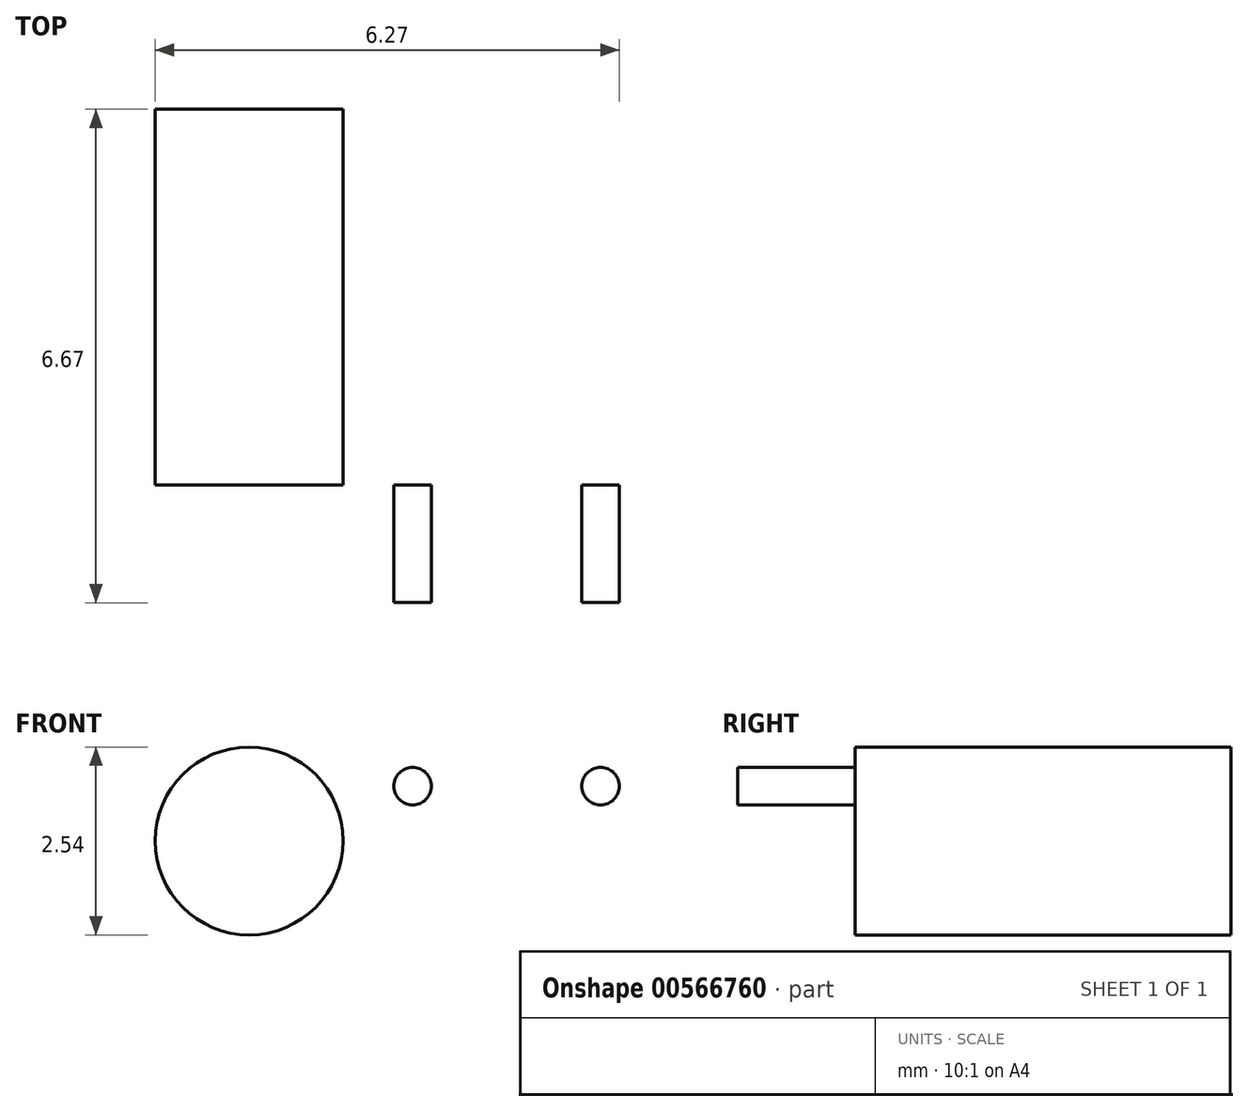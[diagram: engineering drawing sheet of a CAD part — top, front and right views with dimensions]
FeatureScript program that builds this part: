
annotation { "Feature Type Name" : "Feature", "Feature Type Description" : "" }
export const myFeature = defineFeature(function(context is Context, id is Id, definition is map)
    precondition{}
    {
        {
            var Q0;
            Q0=qCreatedBy(makeId("Front.planeOp"),FACE);
            var sketch = newSketch(context, id + "F0", { "sketchPlane" : qUnion([Q0])});
            skCircle(sketch, "E0", {"center": v(0, 0) * mm, "radius": 1.27 * mm});
            skCircle(sketch, "E1", {"center": v(2.2, 0.74) * mm, "radius": 0.25 * mm});
            skSolve(sketch);
        }
        {
            var Q0;
            Q0=makeQuery(id+"F0.imprint","IMPRINT",FACE,{"disambiguationData":[TD([[makeQuery(id+"F0.imprint","IMPRINT",EDGE,{"derivedFrom":sQuery(id+"F0.wireOp",EDGE,"E0")}),1.0]])]});
            extrude(context, id + "F1", {"entities" : qUnion([Q0]), "oppositeDirection" : true, "depth" : 5.08 * mm, "offsetDistance" : 25.4 * mm});
        }
        {
            var Q0;
            Q0=makeQuery(id+"F0.imprint","IMPRINT",FACE,{"disambiguationData":[TD([[makeQuery(id+"F0.imprint","IMPRINT",EDGE,{"derivedFrom":sQuery(id+"F0.wireOp",EDGE,"E1")}),1.0]])]});
            extrude(context, id + "F2", {"entities" : qUnion([Q0]), "depth" : 1.59 * mm, "offsetDistance" : 25.4 * mm});
        }
        {
            var Q0;
            Q0=makeQuery(id+"F2.opExtrude","SWEPT_BODY",BODY,{"disambiguationData":[OSD([sQuery(id+"F0.wireOp",EDGE,"E1")])]});
            transform(context, id + "F3", {"entities" : qUnion([Q0]), "transformType" : TransformType.TRANSLATION_3D, "dx" : 2.54 * mm, "dy" : 0 * mm, "dz" : 0 * mm, "makeCopy" : true});
        }
    });
